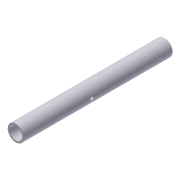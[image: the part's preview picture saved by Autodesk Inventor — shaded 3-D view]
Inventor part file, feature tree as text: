
AUTODESK INVENTOR PART (.ipt)
format: ipt  version: unknown  size: 176,640 bytes
history: native  units: in
note: dims shown in document units (in); Inventor stores cm internally (conversion verified against a paired STEP export)
features: extrude x3, sketch x2, plane x1, thread x1, other x1, projected_geometry x1
ambient origin geometry x8: Origin, YZ Plane, XZ Plane, XY Plane, X Axis, Y Axis, Z Axis, Center Point
feature tree (9):
  extrude  "Extrusion1"  Depth=1.0313in
  plane  "Work Plane1"
  sketch  "Sketch2"  dims[d2=12.0in d3=0.0in d4=0.0in d5=0.25in d6=0.201in d7=5.5in d8=12.0in d9=0.0in d10=12.0in d11=0.0in d12=1.0in d13=0.0in]
  extrude  "Extrusion2"  TaperAngle=0.0deg  [1 undecoded]
  extrude  "Extrusion3"  Depth=0.25in
  thread  "Thread1"  [1 undecoded]
  sketch  "Sketch1"  dims[d0=1.3125in d1=1.0313in]
  other  "Work Axis1"
  projected_geometry  "Projected Loop1"
note: 2 required parameter values undecoded (feature->parameter linkage not recoverable at this tier; creation-order binding heuristic only, values carry confidence <= 0.55)
